# Revit family: 2023835
name_source: partatom
category: Lighting Fixtures
revit_build: Autodesk Revit 2018 (Build: 20170223_1515(x64)
units: mm (PartAtom-declared; Revit-internal decimal feet)

## family parameters
Cut with Voids When Loaded = No
Host = Face
Light Source = No
OmniClass Number = 23.80.70.00
OmniClass Title = Lighting
Part Type = Normal
Room Calculation Point = No
Round Connector Dimension = Use Diameter
Shared = No

## types (1)
- 2023835 OPTIX R 600 2L LUMI HCL TW ALU DA
    Apparent Load = 32 VA
    Assembly Code = D5020200
    AssetType = Fixed
    ClassificationName = Uniclass2015
    ClassificationValue = EF_70_80
    Cost = 0 $
    Default Elevation = 1219 mm
    Description = OPTIX RECESSED 600 2L LUMI HCL TW ALU DALI is a ceiling recessed luminaire for office and education applications with Aluminised plastic extra low glare optics and RAL9016 colour fixture body.  DALI DT8 controlled tunable white light engine.   2700-6200K Tunable White LED, chromaticity tolerance of 3-step MacAdam ellipse. For 2700K - Colour rendering index Ra >98; Melanopic Ratio MEER: 0.526; Fidelity Index Rᶠ: 97; Gamut Index Rᶢ: 103. For 4000K - Colour rendering index Ra >96; Melanopic Ratio MEER: 0.821; Fidelity Index Rᶠ: 95; Gamut Index Rᶢ: 101. For 6200K - Colour rendering index Ra >99; Melanopic Ratio MEER: 1.081; Fidelity Index Rᶠ: 96; Gamut Index Rᶢ: 99. For 4000K luminous flux: 2800lm. Power consumption: 32W. Luminaire efficacy: 88lm/W. UGR<16 Luminance at 65°<200 Cd/m2, IK07, IP20. Photobiological safety risk group 0. Electrical protection Class I. Glow wire test 850°C. 68,000hrs L80B20 lifespan.
    DocumentationLiterature = http://www.sylvania-lighting.com
    DurationUnit = hours
    ElectricShockClassification = 87
    ExpectedLife = 50000
    Height = 38 mm  [stored 0.124672 ft]
    IfcExportAs = Class I
    IfcExportType = IfcLightFixtureType
    ImpactProtectionIndex = IfcLightFixtureType
    IngressProtection = IfcLightFixtureType
    InputNominalFrequency = 4000
    InputVoltage = 0
    LampColourRenderingIndex = 16500
    LampColourTemperature = LED
    LampMacAdamStep = 96
    LampNominalLuminous = 4000 K
    Length = 596 mm  [stored 1.95538 ft]
    LightOutputRatio = LED
    LuminaireType = 0
    ManufacturerName = 87 lm/W
    Material = Feilo Sylvania
    Material_1_FEILO = <By Category>
    Material_2_FEILO = <By Category>
    Material_3_FEILO = <By Category>
    Material_4_FEILO = <By Category>
    Model = OPTIX RECESSED 600 2L LUMI HCL TW ALU DALI
    ModelNumber = 2023835
    ModelReference = OPTIX RECESSED 600 2L LUMI HCL TW ALU DALI
    Name = OPTIX RECESSED 600 2L LUMI HCL TW ALU DALI
    NominalDepth = 596 mm  [stored 1.95538 ft]
    NominalHeight = 38 mm  [stored 0.124672 ft]
    NominalLength = 596 mm  [stored 1.95538 ft]
    PowerConsumption = Lighting
    PowerFactor = 0.95
    Type Image = <None>
    TypeName = OPTIX RECESSED 600 2L LUMI HCL TW ALU DALI
    URL = 0.95
    Voltage = 230 V
    WarrantyDescription = http://www.sylvania-lighting.com
    Width = 596 mm  [stored 1.95538 ft]

note: [stored X ft] marks values corroborated as IEEE doubles in the binary element streams (Revit-internal decimal feet)

## geometry (parser evidence)
native form markers: Sweep x3
no freeform markers — native parametric forms only
